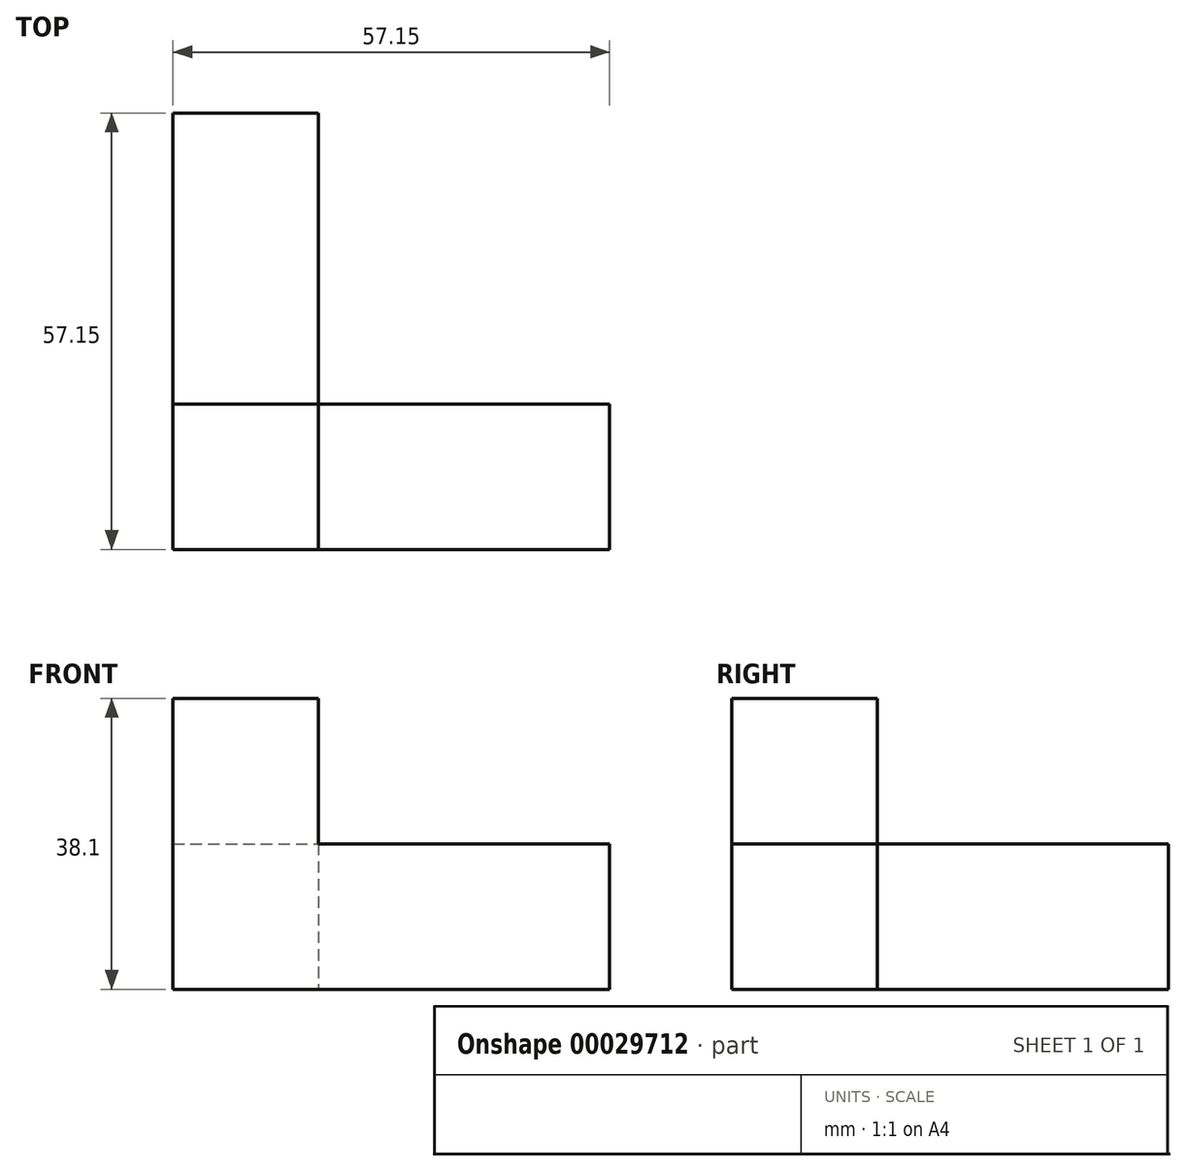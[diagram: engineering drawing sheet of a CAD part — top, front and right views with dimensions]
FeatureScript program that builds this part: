
annotation { "Feature Type Name" : "Feature", "Feature Type Description" : "" }
export const myFeature = defineFeature(function(context is Context, id is Id, definition is map)
    precondition{}
    {
        {
            var Q0;
            Q0=qCreatedBy(makeId("Top.planeOp"),FACE);
            var sketch = newSketch(context, id + "F0", { "sketchPlane" : qUnion([Q0])});
            skLineSegment(sketch, "E0.bottom", {"start": v(-44.92, -38.1) * mm, "end": v(12.23, -38.1) * mm});
            skLineSegment(sketch, "E0.top", {"start": v(-44.92, -57.15) * mm, "end": v(12.23, -57.15) * mm});
            skLineSegment(sketch, "E0.left", {"start": v(-44.92, -38.1) * mm, "end": v(-44.92, -57.15) * mm});
            skLineSegment(sketch, "E0.right", {"start": v(12.23, -38.1) * mm, "end": v(12.23, -57.15) * mm});
            skLineSegment(sketch, "E1.bottom", {"start": v(-44.92, -38.1) * mm, "end": v(-25.87, -38.1) * mm});
            skLineSegment(sketch, "E1.top", {"start": v(-44.92, 0) * mm, "end": v(-25.87, 0) * mm});
            skLineSegment(sketch, "E1.left", {"start": v(-44.92, -38.1) * mm, "end": v(-44.92, 0) * mm});
            skLineSegment(sketch, "E1.right", {"start": v(-25.87, -38.1) * mm, "end": v(-25.87, 0) * mm});
            skSolve(sketch);
        }
        {
            var Q0;
            Q0 = qSketchRegion(id + "F0", true);
            extrude(context, id + "F1", {"entities" : qUnion([Q0]), "depth" : 19.05 * mm});
        }
        {
            var Q0;
            Q0=makeQuery(id+"F1.opExtrude","CAP_FACE",FACE,{"disambiguationData":[OSD([sQuery(id+"F0.wireOp",EDGE,"E0.bottom"),sQuery(id+"F0.wireOp",EDGE,"E0.top"),sQuery(id+"F0.wireOp",EDGE,"E0.left"),sQuery(id+"F0.wireOp",EDGE,"E0.right"),sQuery(id+"F0.wireOp",EDGE,"E1.top"),sQuery(id+"F0.wireOp",EDGE,"E1.left"),sQuery(id+"F0.wireOp",EDGE,"E1.right")])],"isStart":false});
            var sketch = newSketch(context, id + "F2", { "sketchPlane" : qUnion([Q0])});
            skLineSegment(sketch, "E2.bottom", {"start": v(-44.92, -57.15) * mm, "end": v(-25.87, -57.15) * mm});
            skLineSegment(sketch, "E2.top", {"start": v(-44.92, -38.1) * mm, "end": v(-25.87, -38.1) * mm});
            skLineSegment(sketch, "E2.left", {"start": v(-44.92, -57.15) * mm, "end": v(-44.92, -38.1) * mm});
            skLineSegment(sketch, "E2.right", {"start": v(-25.87, -57.15) * mm, "end": v(-25.87, -38.1) * mm});
            skSolve(sketch);
        }
        {
            var Q0;
            Q0 = qSketchRegion(id + "F2", true);
            extrude(context, id + "F3", {"entities" : qUnion([Q0]), "operationType" : NewBodyOperationType.ADD, "depth" : 19.05 * mm});
        }
    });
